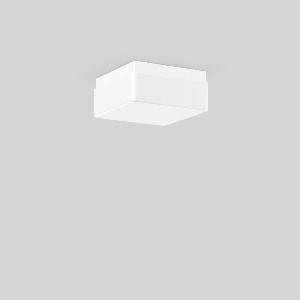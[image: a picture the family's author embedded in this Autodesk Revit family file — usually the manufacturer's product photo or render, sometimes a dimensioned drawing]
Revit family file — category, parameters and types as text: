
# Revit family: quadrat_21128_002_5cfc
name_source: partatom
category: Lighting Fixtures
units: mm (PartAtom-declared; Revit-internal decimal feet)

## family parameters
Cut with Voids When Loaded = No
Host = Face
Light Source = No
Part Type = Normal
Room Calculation Point = No
Round Connector Dimension = Use Diameter
Shared = No

## types (1)
- QUADRAT (1 x QA60/clear E27, 915 lm, 57 W, 3000)
    Apparent Load = 57 VA
    CIE Flux Codes = 35 64 86 74 50
    Color Rendering = 90
    Color Temperature = 3000
    Default Elevation = 1800 mm
    Description = Series: QUADRAT
Square surface-mounted luminaire in classic design. Base: plastic. Opal glass: mouth-blown, satin finish. Diffuser fastening: spring system. Suitable for Ceiling mounting, Wall (surface). IP 43 ceiling mounting, IP 44 wall mounting. 
Colour: white
Length: 240 mm
Width: 240 mm
Height: 110 mm
Lamp: A60
Number of lamps: 1
Wattage: 75 W
Socket: E27
System power: 60 W
Rated luminous flux: 370 lm
Luminous efficiency: 6 lm/W
Control gear: Converter not necessary
Protection class: II
Type of protection: IP 43
    Height = 110 mm
    Lamp = 1 x QA60/clear E27
    Lamp Light Flux = 915 lm
    Lamp Power = 57 W
    Lamp count = 1
    Length = 240 mm
    Lifetime = 3000 h
    Luminous efficacy = 8 lm/W
    Manufacturer = RZB
    ModVariant = No
    Model = 21128.002
    Mounting Place = Ceiling, Wall
    Mounting Type = Surface mounted
    Number of Poles = 1
    OnlyDefault = Yes
    Power Factor = 1
    Product Name = QUADRAT
    Product group = Surface mounted ceiling and wall luminaires
    ProductGroupID = 305
    Protection Class = Protection class II
    Protection Degree = IP 43
    RLX_Detail_Level = 1
    RLX_Emergency_Light_Flux = 0 lm
    RLX_Emergency_Type = 0
    RLX_Emergency_Type_DB = No
    RlxData = <blob elided: 10041 chars, md5=91c2854b>
    Socket = E27
    Standby Power = 0 W
    System Light Flux = 460 lm
    System Power = 57 W
    Type Comments = Product without accessories
    Type Image = 21128.002.jpg
    URL = http://relux.com
    VarID = ---
    Voltage = 230 V
    Voltage Range = 220-240 V
    Weight = 0.00 kg
    Width = 240 mm

## geometry (parser evidence)
native form markers: Sweep x13
no freeform markers — native parametric forms only
